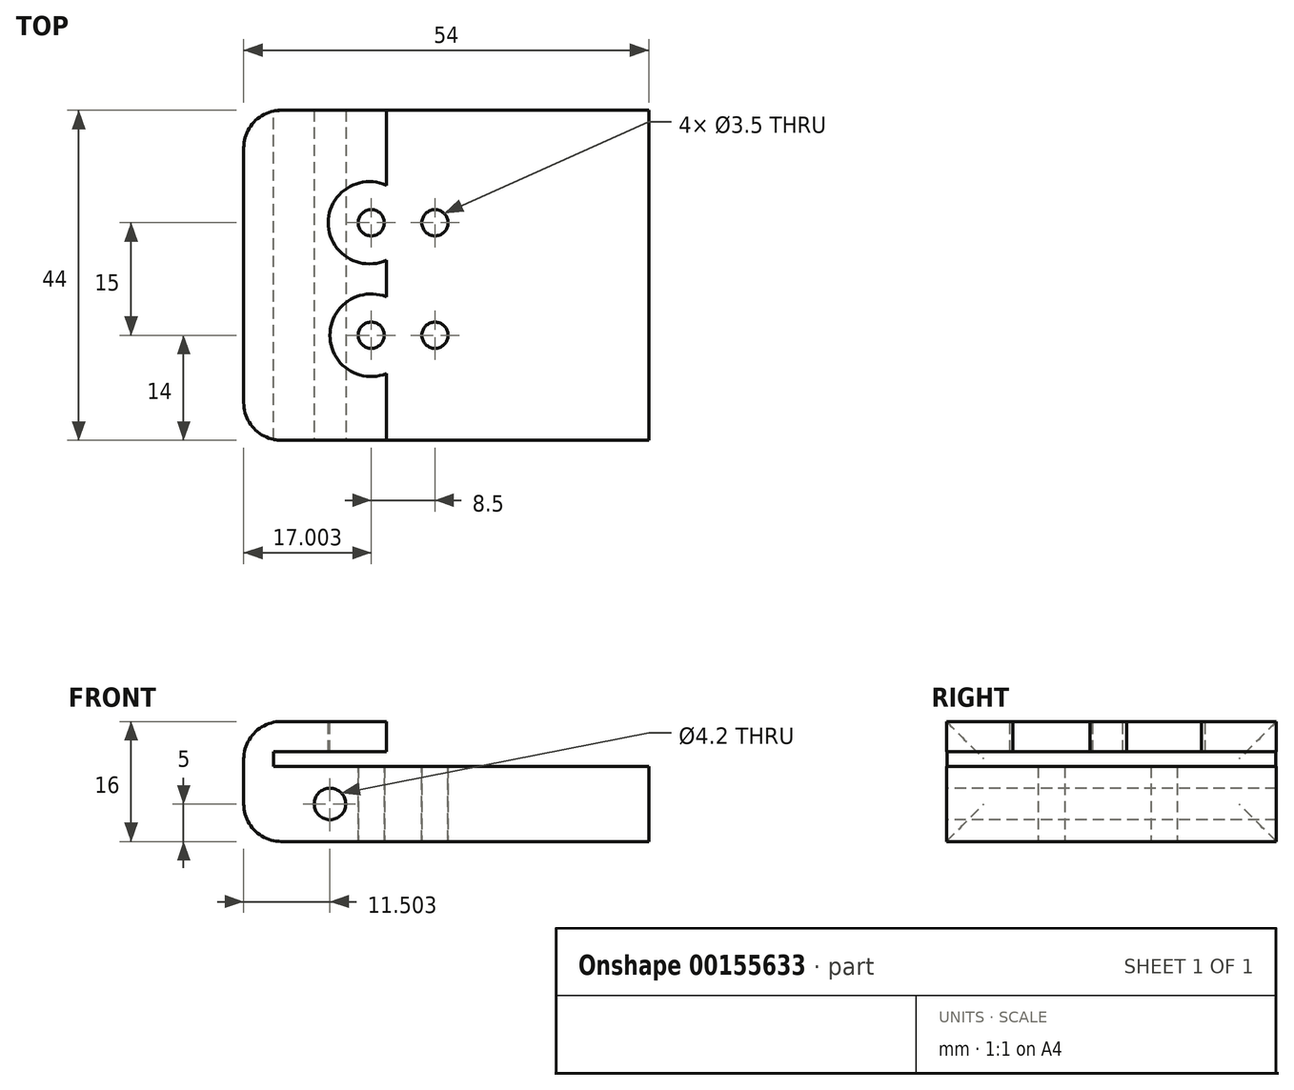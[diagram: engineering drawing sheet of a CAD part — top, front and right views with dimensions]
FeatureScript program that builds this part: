
annotation { "Feature Type Name" : "Feature", "Feature Type Description" : "" }
export const myFeature = defineFeature(function(context is Context, id is Id, definition is map)
    precondition{}
    {
        {
            var Q0;
            Q0=qCreatedBy(makeId("Front.planeOp"),FACE);
            var sketch = newSketch(context, id + "F0", { "sketchPlane" : qUnion([Q0])});
            skLineSegment(sketch, "E0.bottom", {"start": v(-28.86, 0) * mm, "end": v(25.14, 0) * mm});
            skLineSegment(sketch, "E0.top", {"start": v(-28.86, -10) * mm, "end": v(25.14, -10) * mm});
            skLineSegment(sketch, "E0.left", {"start": v(-28.86, 0) * mm, "end": v(-28.86, -10) * mm});
            skLineSegment(sketch, "E0.right", {"start": v(25.14, 0) * mm, "end": v(25.14, -10) * mm});
            skLineSegment(sketch, "E1.bottom", {"start": v(-28.86, 0) * mm, "end": v(-24.86, 0) * mm});
            skLineSegment(sketch, "E1.top", {"start": v(-28.86, 6) * mm, "end": v(-24.86, 6) * mm});
            skLineSegment(sketch, "E1.left", {"start": v(-28.86, 0) * mm, "end": v(-28.86, 6) * mm});
            skLineSegment(sketch, "E1.right", {"start": v(-24.86, 0) * mm, "end": v(-24.86, 6) * mm});
            skLineSegment(sketch, "E2.bottom", {"start": v(-24.86, 6) * mm, "end": v(-9.86, 6) * mm});
            skLineSegment(sketch, "E2.top", {"start": v(-24.86, 2) * mm, "end": v(-9.86, 2) * mm});
            skLineSegment(sketch, "E2.left", {"start": v(-24.86, 6) * mm, "end": v(-24.86, 2) * mm});
            skLineSegment(sketch, "E2.right", {"start": v(-9.86, 6) * mm, "end": v(-9.86, 2) * mm});
            skSolve(sketch);
        }
        {
            var Q0;
            Q0 = qSketchRegion(id + "F0", true);
            extrude(context, id + "F1", {"entities" : qUnion([Q0]), "depth" : 44 * mm});
        }
        {
            var Q0;
            Q0=makeQuery(id+"F1.opExtrude","SWEPT_FACE",FACE,{"disambiguationData":[OSD([sQuery(id+"F0.wireOp",EDGE,"E0.top")])]});
            var sketch = newSketch(context, id + "F2", { "sketchPlane" : qUnion([Q0])});
            skPoint(sketch, "E3", {"position": v(-11.86, 15) * mm});
            skPoint(sketch, "E4", {"position": v(-3.36, 30) * mm});
            skSolve(sketch);
        }
        {
            var Q0;
            Q0=sQuery(id+"F2.wireOp",VERTEX,"E3");
            var Q1;
            Q1=sQuery(id+"F2.wireOp",VERTEX,"E4");
            var Q2;
            Q2=makeQuery(id+"F1.opExtrude","SWEPT_BODY",BODY,{"disambiguationData":[OSD([sQuery(id+"F0.wireOp",EDGE,"E0.bottom"),sQuery(id+"F0.wireOp",EDGE,"E0.top"),sQuery(id+"F0.wireOp",EDGE,"E0.left"),sQuery(id+"F0.wireOp",EDGE,"E0.right"),sQuery(id+"F0.wireOp",EDGE,"E1.top"),sQuery(id+"F0.wireOp",EDGE,"E1.left"),sQuery(id+"F0.wireOp",EDGE,"E1.right"),sQuery(id+"F0.wireOp",EDGE,"E2.bottom"),sQuery(id+"F0.wireOp",EDGE,"E2.top"),sQuery(id+"F0.wireOp",EDGE,"E2.right")])]});
            hole(context, id + "F3", {"style" : HoleStyle.SIMPLE, "endStyle" : HoleEndStyle.THROUGH, "holeDiameter" : 3.5 * mm, "locations" : qUnion([Q0, Q1]), "scope" : qUnion([Q2]), "isTappedThrough" : true});
        }
        {
            var Q0;
            Q0=makeQuery(id+"F1.opExtrude","SWEPT_FACE",FACE,{"disambiguationData":[OSD([sQuery(id+"F0.wireOp",EDGE,"E1.top"),sQuery(id+"F0.wireOp",EDGE,"E2.bottom")])]});
            var sketch = newSketch(context, id + "F4", { "sketchPlane" : qUnion([Q0])});
            skArc(sketch, "E5", {"start": v(-9.86, -10) * mm, "mid": v(-17.6, -15) * mm, "end": v(-9.86, -20) * mm});
            skSolve(sketch);
        }
        {
            var Q0;
            {var subQ0=sQuery(id+"F4.wireOp",EDGE,"E5");Q0=makeQuery(id+"F4.imprint","IMPRINT",FACE,{"disambiguationData":[TD([[makeQuery(id+"F4.imprint","IMPRINT",EDGE,{"derivedFrom":subQ0}),1.0]])]});}
            extrude(context, id + "F5", {"entities" : qUnion([Q0]), "operationType" : NewBodyOperationType.REMOVE, "oppositeDirection" : true, "depth" : 4 * mm});
        }
        {
            var Q0;
            Q0=makeQuery(id+"F1.opExtrude","CAP_FACE",FACE,{"disambiguationData":[OSD([sQuery(id+"F0.wireOp",EDGE,"E0.bottom"),sQuery(id+"F0.wireOp",EDGE,"E0.top"),sQuery(id+"F0.wireOp",EDGE,"E0.left"),sQuery(id+"F0.wireOp",EDGE,"E0.right"),sQuery(id+"F0.wireOp",EDGE,"E1.top"),sQuery(id+"F0.wireOp",EDGE,"E1.left"),sQuery(id+"F0.wireOp",EDGE,"E1.right"),sQuery(id+"F0.wireOp",EDGE,"E2.bottom"),sQuery(id+"F0.wireOp",EDGE,"E2.top"),sQuery(id+"F0.wireOp",EDGE,"E2.right")])],"isStart":false});
            var sketch = newSketch(context, id + "F6", { "sketchPlane" : qUnion([Q0])});
            skLineSegment(sketch, "E6", {"start": v(-28.86, -5) * mm, "end": v(-5.86, -5) * mm});
            skLineSegment(sketch, "E7", {"start": v(-17.36, 0) * mm, "end": v(-17.36, -10) * mm});
            skPoint(sketch, "E7.startSnap0", {"position": v(-17.36, -5) * mm});
            skSolve(sketch);
        }
        {
            var Q0;
            Q0=sQuery(id+"F6.wireOp",VERTEX,"E7.startSnap0");
            var Q1;
            Q1=makeQuery(id+"F1.opExtrude","SWEPT_BODY",BODY,{"disambiguationData":[OSD([sQuery(id+"F0.wireOp",EDGE,"E0.bottom"),sQuery(id+"F0.wireOp",EDGE,"E0.top"),sQuery(id+"F0.wireOp",EDGE,"E0.left"),sQuery(id+"F0.wireOp",EDGE,"E0.right"),sQuery(id+"F0.wireOp",EDGE,"E1.top"),sQuery(id+"F0.wireOp",EDGE,"E1.left"),sQuery(id+"F0.wireOp",EDGE,"E1.right"),sQuery(id+"F0.wireOp",EDGE,"E2.bottom"),sQuery(id+"F0.wireOp",EDGE,"E2.top"),sQuery(id+"F0.wireOp",EDGE,"E2.right")])]});
            hole(context, id + "F7", {"style" : HoleStyle.SIMPLE, "endStyle" : HoleEndStyle.THROUGH, "holeDiameter" : 4.2 * mm, "locations" : qUnion([Q0]), "scope" : qUnion([Q1]), "isTappedThrough" : true});
        }
        {
            var Q0;
            Q0=makeQuery(id+"F1.opExtrude","SWEPT_FACE",FACE,{"disambiguationData":[OSD([sQuery(id+"F0.wireOp",EDGE,"E0.bottom")])]});
            var sketch = newSketch(context, id + "F8", { "sketchPlane" : qUnion([Q0])});
            skLineSegment(sketch, "E8.bottom", {"start": v(-11.86, -15) * mm, "end": v(-3.36, -15) * mm});
            skLineSegment(sketch, "E8.top", {"start": v(-11.86, -30) * mm, "end": v(-3.36, -30) * mm});
            skLineSegment(sketch, "E8.left", {"start": v(-11.86, -15) * mm, "end": v(-11.86, -30) * mm});
            skLineSegment(sketch, "E8.right", {"start": v(-3.36, -15) * mm, "end": v(-3.36, -30) * mm});
            skLineSegment(sketch, "E9", {"start": v(-7.6, -4.4) * mm, "end": v(-7.6, -35.7) * mm});
            skLineSegment(sketch, "E10", {"start": v(-19.54, -22.5) * mm, "end": v(8.07, -22.5) * mm});
            skSolve(sketch);
        }
        {
            var Q0;
            Q0=sQuery(id+"F8.wireOp",VERTEX,"E8.right.start");
            var Q1;
            Q1=sQuery(id+"F8.wireOp",VERTEX,"E8.left.end");
            var Q2;
            Q2=makeQuery(id+"F1.opExtrude","SWEPT_BODY",BODY,{"disambiguationData":[OSD([sQuery(id+"F0.wireOp",EDGE,"E0.bottom"),sQuery(id+"F0.wireOp",EDGE,"E0.top"),sQuery(id+"F0.wireOp",EDGE,"E0.left"),sQuery(id+"F0.wireOp",EDGE,"E0.right"),sQuery(id+"F0.wireOp",EDGE,"E1.top"),sQuery(id+"F0.wireOp",EDGE,"E1.left"),sQuery(id+"F0.wireOp",EDGE,"E1.right"),sQuery(id+"F0.wireOp",EDGE,"E2.bottom"),sQuery(id+"F0.wireOp",EDGE,"E2.top"),sQuery(id+"F0.wireOp",EDGE,"E2.right")])]});
            hole(context, id + "F9", {"style" : HoleStyle.SIMPLE, "endStyle" : HoleEndStyle.THROUGH, "holeDiameter" : 3.5 * mm, "locations" : qUnion([Q0, Q1]), "scope" : qUnion([Q2]), "isTappedThrough" : true});
        }
        {
            var Q0;
            Q0=makeQuery(id+"F1.opExtrude","SWEPT_FACE",FACE,{"disambiguationData":[OSD([sQuery(id+"F0.wireOp",EDGE,"E1.top"),sQuery(id+"F0.wireOp",EDGE,"E2.bottom")])]});
            var sketch = newSketch(context, id + "F10", { "sketchPlane" : qUnion([Q0])});
            skPoint(sketch, "E11", {"position": v(-11.86, -30) * mm});
            skArc(sketch, "E12", {"start": v(-9.86, -24.87) * mm, "mid": v(-17.36, -30) * mm, "end": v(-9.86, -35.13) * mm});
            skSolve(sketch);
        }
        {
            var Q0;
            {var subQ0=sQuery(id+"F10.wireOp",EDGE,"E12");Q0=makeQuery(id+"F10.imprint","IMPRINT",FACE,{"disambiguationData":[TD([[makeQuery(id+"F10.imprint","IMPRINT",EDGE,{"derivedFrom":subQ0}),1.0]])]});}
            extrude(context, id + "F11", {"entities" : qUnion([Q0]), "operationType" : NewBodyOperationType.REMOVE, "endBound" : BoundingType.UP_TO_NEXT, "oppositeDirection" : true, "depth" : 25 * mm});
        }
        {
            var Q0;
            Q0=makeQuery(id+"F1.opExtrude","SWEPT_FACE",FACE,{"disambiguationData":[OSD([sQuery(id+"F0.wireOp",EDGE,"E0.left"),sQuery(id+"F0.wireOp",EDGE,"E1.left")])]});
            fillet(context, id + "F12", {"entities" : qUnion([Q0]), "radius" : 5 * mm, "tangentPropagation" : true, "allowEdgeOverflow" : false});
        }
    });
